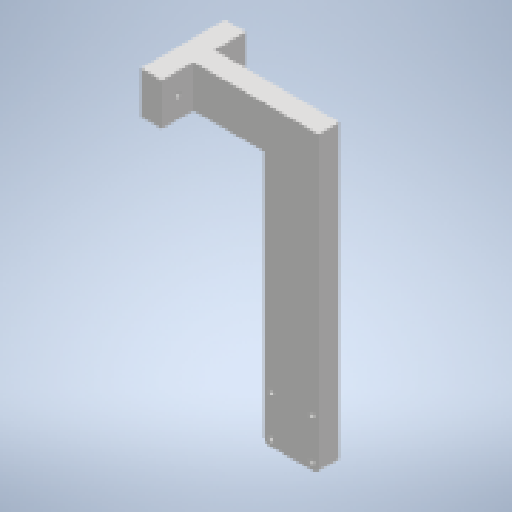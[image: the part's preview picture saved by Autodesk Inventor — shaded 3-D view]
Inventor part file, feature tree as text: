
AUTODESK INVENTOR PART (.ipt)
format: ipt  version: 2023 (Build 270158000, 158)  size: 177,664 bytes
history: native  units: mm
features: reference x8, other x5, sheet_metal_op x3, sketch x2
ambient origin geometry x8: Origin, YZ Plane, XZ Plane, XY Plane, X Axis, Y Axis, Z Axis, Center Point
bodies: Solid1 (feature_tree)
feature tree (18):
  sheet_metal_op  "Face1"
  sheet_metal_op  "Face2"
  sketch  "Sketch1"  dims[d0=350.0mm]
  reference  "Reference1"
  reference  "Reference2"
  reference  "Reference3"
  reference  "Reference4"
  reference  "Reference5"
  reference  "Reference6"
  reference  "Reference7"
  reference  "Reference8"
  other  "Plate1"
  sketch  "Sketch2"  dims[d1=300.0mm d2=5.0mm d3=25.0mm d4=50.0mm d5=50.0mm d6=25.0mm d7=20.0mm d8=20.0mm d9=6.0mm d10=25.0mm d11=25.0mm d12=12.5mm d13=50.0mm d14=25.0mm]
  other  "Plate2"
  sheet_metal_op  "Bend1"
  other  "ensamble_general.iam"
  other  "patas:3"
  other  "lamina:1"
